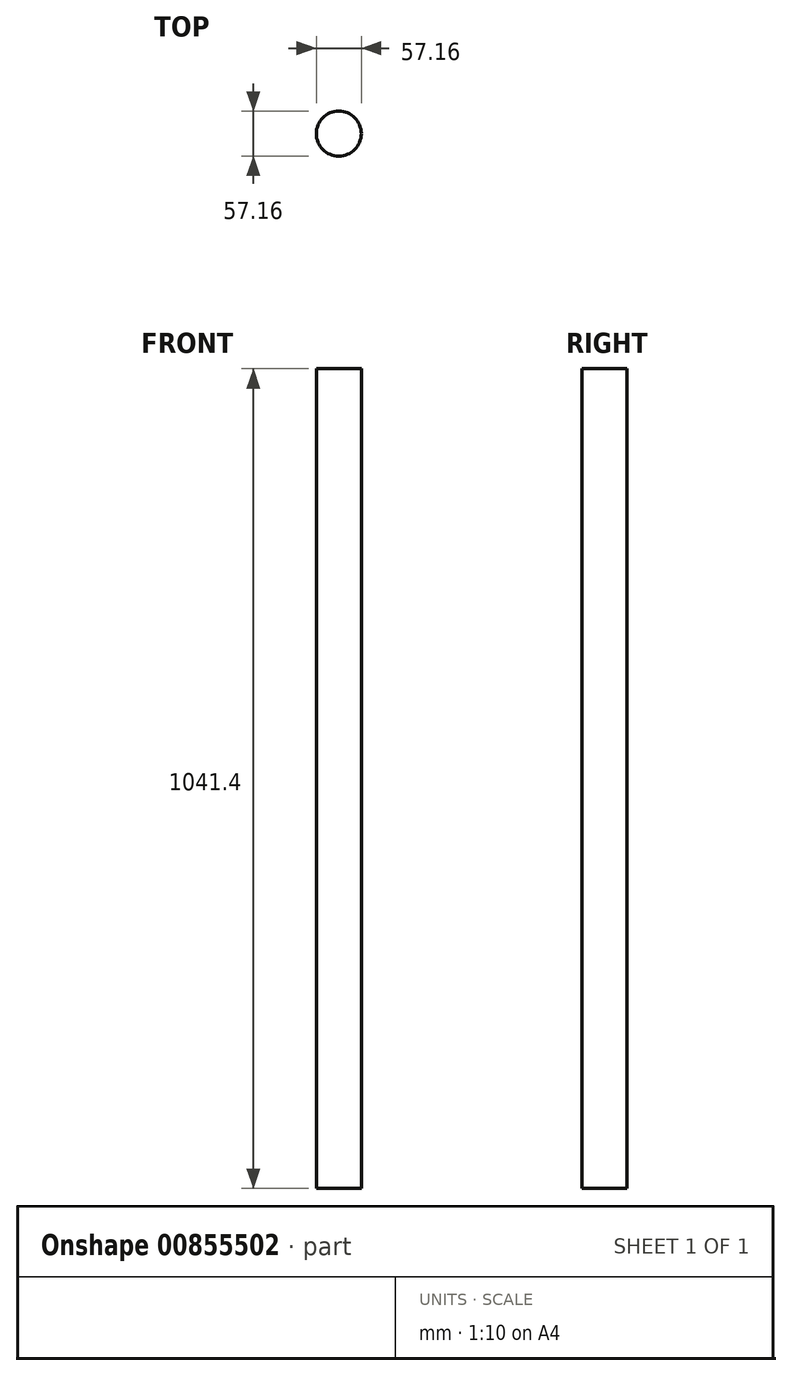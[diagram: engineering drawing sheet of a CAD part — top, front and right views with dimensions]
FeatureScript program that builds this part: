
annotation { "Feature Type Name" : "Feature", "Feature Type Description" : "" }
export const myFeature = defineFeature(function(context is Context, id is Id, definition is map)
    precondition{}
    {
        {
            var Q0;
            Q0=qCreatedBy(makeId("Top.planeOp"),FACE);
            var sketch = newSketch(context, id + "F0", { "sketchPlane" : qUnion([Q0])});
            skCircle(sketch, "E0", {"center": v(0, 0) * mm, "radius": 28.58 * mm});
            skSolve(sketch);
        }
        {
            var Q0;
            Q0=makeQuery(id+"F0.imprint","IMPRINT",FACE,{"disambiguationData":[TD([[makeQuery(id+"F0.imprint","IMPRINT",EDGE,{"derivedFrom":sQuery(id+"F0.wireOp",EDGE,"E0")}),1.0]])]});
            extrude(context, id + "F1", {"entities" : qUnion([Q0]), "depth" : 1041.4 * mm, "offsetDistance" : 25.4 * mm});
        }
    });
